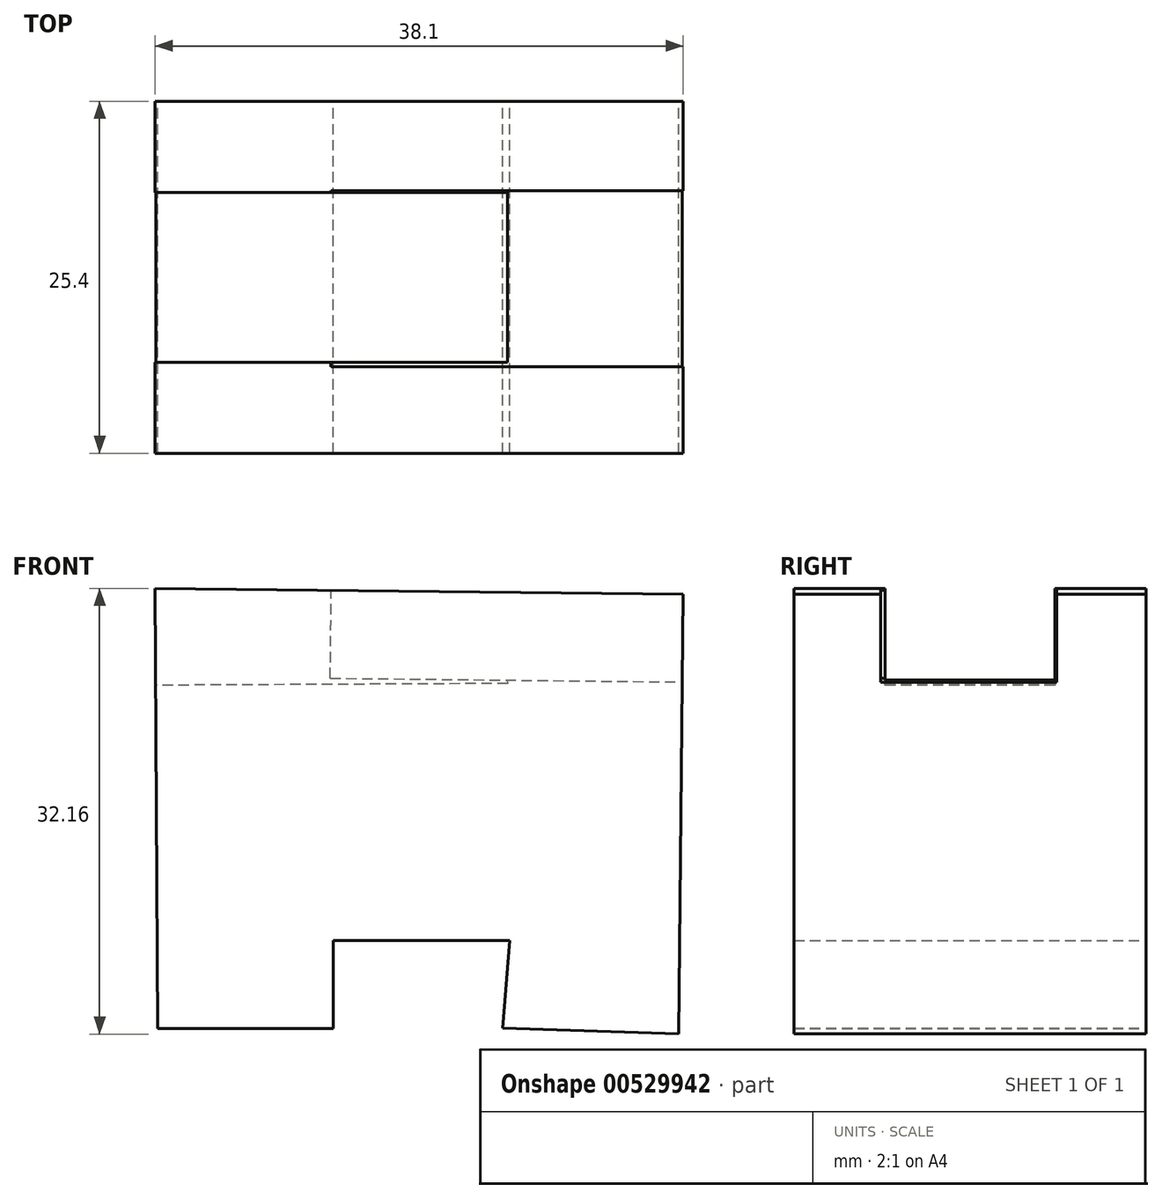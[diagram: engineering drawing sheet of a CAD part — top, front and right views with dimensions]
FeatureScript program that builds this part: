
annotation { "Feature Type Name" : "Feature", "Feature Type Description" : "" }
export const myFeature = defineFeature(function(context is Context, id is Id, definition is map)
    precondition{}
    {
        {
            var Q0;
            Q0=qCreatedBy(makeId("Front.planeOp"),FACE);
            var sketch = newSketch(context, id + "F0", { "sketchPlane" : qUnion([Q0])});
            skLineSegment(sketch, "E0", {"start": v(-58, 11.4) * mm, "end": v(-45.3, 11.4) * mm});
            skLineSegment(sketch, "E1", {"start": v(-45.3, 11.4) * mm, "end": v(-45.3, 17.74) * mm});
            skLineSegment(sketch, "E2", {"start": v(-45.3, 17.74) * mm, "end": v(-32.6, 17.74) * mm});
            skLineSegment(sketch, "E3", {"start": v(-33.1, 11.41) * mm, "end": v(-20.4, 10.98) * mm});
            skLineSegment(sketch, "E4", {"start": v(-20.4, 10.98) * mm, "end": v(-20.07, 42.73) * mm});
            skLineSegment(sketch, "E5", {"start": v(-20.07, 42.73) * mm, "end": v(-58.17, 43.14) * mm});
            skLineSegment(sketch, "E6", {"start": v(-58.17, 43.14) * mm, "end": v(-58, 11.4) * mm});
            skLineSegment(sketch, "E7", {"start": v(-32.6, 17.74) * mm, "end": v(-33.1, 11.41) * mm});
            skSolve(sketch);
        }
        {
            var Q0;
            Q0=makeQuery(id+"F0.imprint","IMPRINT",FACE,{"disambiguationData":[TD([[makeQuery(id+"F0.imprint","IMPRINT",EDGE,{"derivedFrom":sQuery(id+"F0.wireOp",EDGE,"E0")}),1.0]])]});
            extrude(context, id + "F1", {"entities" : qUnion([Q0]), "depth" : 25.4 * mm, "offsetDistance" : 25.4 * mm});
        }
        {
            var Q0;
            Q0=makeQuery(id+"F1.opExtrude","SWEPT_FACE",FACE,{"disambiguationData":[OSD([sQuery(id+"F0.wireOp",EDGE,"E6")])]});
            var sketch = newSketch(context, id + "F2", { "sketchPlane" : qUnion([Q0])});
            skLineSegment(sketch, "E8", {"start": v(0, 36.44) * mm, "end": v(25.4, 36.44) * mm});
            skLineSegment(sketch, "E9", {"start": v(25.4, 36.44) * mm, "end": v(18.83, 36.44) * mm});
            skLineSegment(sketch, "E10", {"start": v(18.83, 36.44) * mm, "end": v(18.83, 43.44) * mm});
            skLineSegment(sketch, "E11", {"start": v(18.83, 43.44) * mm, "end": v(0, 43.44) * mm});
            skLineSegment(sketch, "E12", {"start": v(0, 43.44) * mm, "end": v(0, 36.44) * mm});
            skLineSegment(sketch, "E13", {"start": v(6.58, 36.44) * mm, "end": v(6.58, 43.44) * mm});
            skLineSegment(sketch, "E14", {"start": v(6.58, 43.44) * mm, "end": v(25.4, 43.44) * mm});
            skLineSegment(sketch, "E15", {"start": v(25.4, 43.44) * mm, "end": v(25.4, 36.44) * mm});
            skSolve(sketch);
        }
        {
            var Q0;
            {var subQ0=sQuery(id+"F2.wireOp",EDGE,"E10");Q0=makeQuery(id+"F2.imprint","IMPRINT",FACE,{"disambiguationData":[TD([[makeQuery(id+"F2.imprint","IMPRINT",EDGE,{"derivedFrom":subQ0}),1.0]])]});}
            extrude(context, id + "F3", {"entities" : qUnion([Q0]), "operationType" : NewBodyOperationType.REMOVE, "oppositeDirection" : true, "depth" : 25.4 * mm, "offsetDistance" : 25.4 * mm});
        }
        {
            var Q0;
            Q0=makeQuery(id+"F1.opExtrude","SWEPT_FACE",FACE,{"disambiguationData":[OSD([sQuery(id+"F0.wireOp",EDGE,"E4")])]});
            var sketch = newSketch(context, id + "F4", { "sketchPlane" : qUnion([Q0])});
            skLineSegment(sketch, "E16", {"start": v(-19.15, 42.51) * mm, "end": v(-19.15, 36.16) * mm});
            skLineSegment(sketch, "E17", {"start": v(-19.15, 36.16) * mm, "end": v(-6.45, 36.16) * mm});
            skLineSegment(sketch, "E18", {"start": v(-6.45, 36.16) * mm, "end": v(-6.45, 42.51) * mm});
            skLineSegment(sketch, "E19", {"start": v(-6.45, 42.51) * mm, "end": v(0, 42.51) * mm});
            skLineSegment(sketch, "E20", {"start": v(0, 42.51) * mm, "end": v(0, 36.16) * mm});
            skLineSegment(sketch, "E21", {"start": v(0, 36.16) * mm, "end": v(-6.45, 36.16) * mm});
            skLineSegment(sketch, "E22", {"start": v(-25.4, 36.16) * mm, "end": v(-25.4, 42.51) * mm});
            skPoint(sketch, "E22.startSnap0", {"position": v(-12.8, 36.16) * mm});
            skLineSegment(sketch, "E23", {"start": v(-25.4, 42.51) * mm, "end": v(-25.4, 36.16) * mm});
            skLineSegment(sketch, "E24", {"start": v(-19.15, 36.16) * mm, "end": v(-25.4, 36.16) * mm});
            skSolve(sketch);
        }
        {
            var Q0;
            {var subQ0=sQuery(id+"F4.wireOp",EDGE,"E16");Q0=makeQuery(id+"F4.imprint","IMPRINT",FACE,{"disambiguationData":[TD([[makeQuery(id+"F4.imprint","IMPRINT",EDGE,{"derivedFrom":subQ0}),1.0]])]});}
            extrude(context, id + "F5", {"entities" : qUnion([Q0]), "operationType" : NewBodyOperationType.REMOVE, "oppositeDirection" : true, "depth" : 25.4 * mm, "offsetDistance" : 25.4 * mm});
        }
    });
